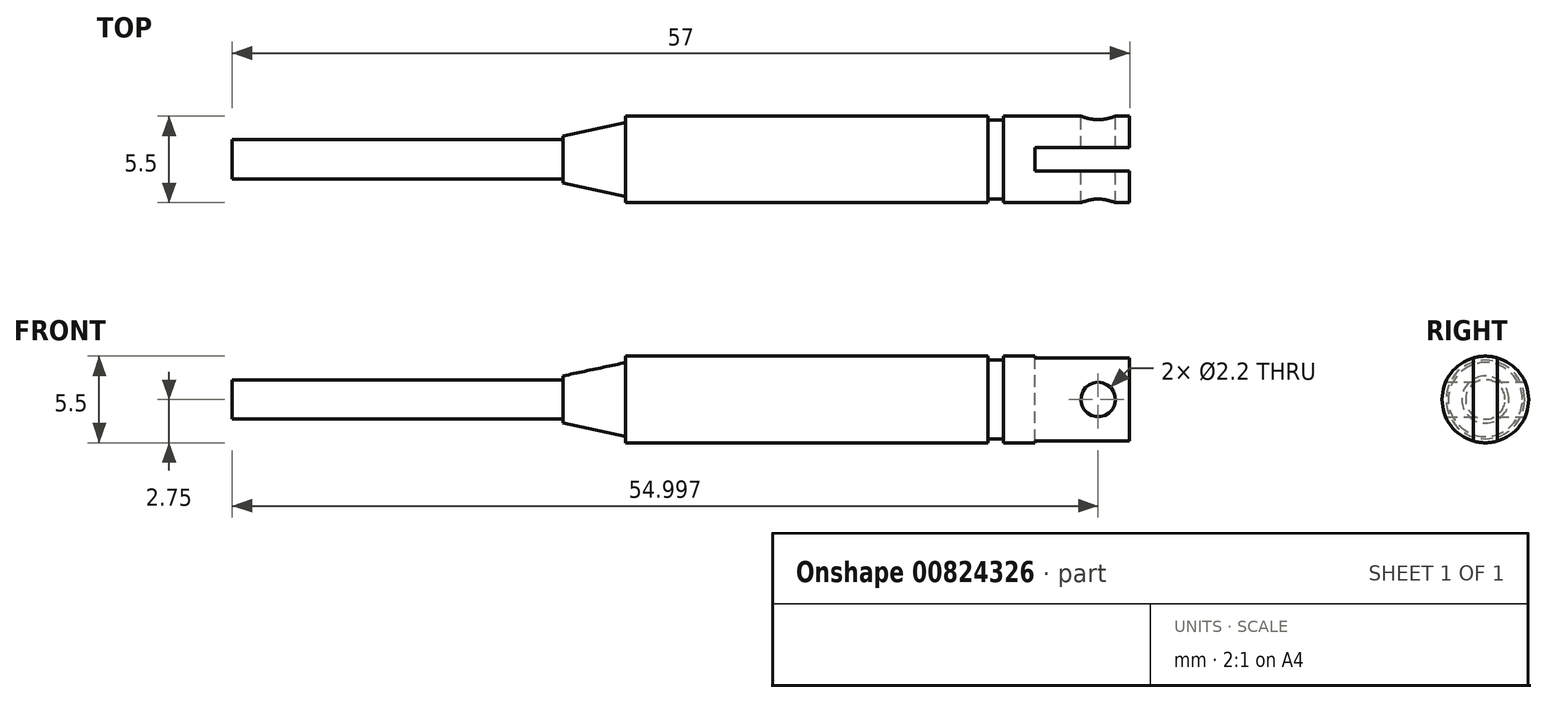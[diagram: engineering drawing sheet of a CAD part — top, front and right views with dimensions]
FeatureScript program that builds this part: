
annotation { "Feature Type Name" : "Feature", "Feature Type Description" : "" }
export const myFeature = defineFeature(function(context is Context, id is Id, definition is map)
    precondition{}
    {
        {
            var Q0;
            Q0=qCreatedBy(makeId("Front.planeOp"),FACE);
            var sketch = newSketch(context, id + "F0", { "sketchPlane" : qUnion([Q0])});
            skLineSegment(sketch, "E0.bottom", {"start": v(-27.2, 2.75) * mm, "end": v(-2.2, 2.75) * mm, "construction": true});
            skLineSegment(sketch, "E0.top", {"start": v(-27.2, 0) * mm, "end": v(29.8, 0) * mm});
            skLineSegment(sketch, "E0.left", {"start": v(-27.2, 2.75) * mm, "end": v(-27.2, 1.25) * mm, "construction": true});
            skLineSegment(sketch, "E0.right", {"start": v(29.8, 2.75) * mm, "end": v(29.8, 0) * mm});
            skLineSegment(sketch, "E1", {"start": v(-2.2, 2.75) * mm, "end": v(-2.2, 2.35) * mm});
            skLineSegment(sketch, "E2.bottom", {"start": v(-27.2, 1.25) * mm, "end": v(-27.2, 1.25) * mm});
            skLineSegment(sketch, "E2.top", {"start": v(-27.2, 0) * mm, "end": v(-2.2, 0) * mm});
            skLineSegment(sketch, "E2.left", {"start": v(-27.2, 1.25) * mm, "end": v(-27.2, 0) * mm});
            skLineSegment(sketch, "E2.right", {"start": v(-2.2, 1.25) * mm, "end": v(-2.2, 0) * mm});
            skLineSegment(sketch, "E3", {"start": v(-6.2, 1.25) * mm, "end": v(-6.2, 1.5) * mm});
            skLineSegment(sketch, "E4", {"start": v(-6.2, 1.5) * mm, "end": v(-2.2, 2.35) * mm});
            skLineSegment(sketch, "E5", {"start": v(-6.2, 1.25) * mm, "end": v(-2.2, 1.25) * mm, "construction": true});
            skLineSegment(sketch, "E6", {"start": v(-2.2, 2.35) * mm, "end": v(-2.2, 0) * mm, "construction": true});
            skLineSegment(sketch, "E7", {"start": v(-27.2, 1.25) * mm, "end": v(-6.2, 1.25) * mm});
            skLineSegment(sketch, "E8", {"start": v(29.8, 2.75) * mm, "end": v(21.8, 2.75) * mm});
            skLineSegment(sketch, "E9", {"start": v(20.8, 2.75) * mm, "end": v(-2.2, 2.75) * mm});
            skLineSegment(sketch, "E10", {"start": v(21.8, 2.75) * mm, "end": v(21.8, 2.5) * mm});
            skLineSegment(sketch, "E11", {"start": v(21.8, 2.5) * mm, "end": v(20.8, 2.5) * mm});
            skLineSegment(sketch, "E12", {"start": v(20.8, 2.5) * mm, "end": v(20.8, 2.75) * mm});
            skSolve(sketch);
        }
        {
            var Q0;
            Q0 = qSketchRegion(id + "F0", true);
            var Q1;
            Q1=sQuery(id+"F0.wireOp",EDGE,"E0.top");
            revolve(context, id + "F1", {"surfaceOperationType" : NewSurfaceOperationType.NEW, "entities" : qUnion([Q0]), "axis" : qUnion([Q1]), "revolveType" : RevolveType.FULL});
        }
        {
            var Q0;
            Q0=makeQuery(id+"F1.opRevolve","SWEPT_FACE",FACE,{"disambiguationData":[OSD([sQuery(id+"F0.wireOp",EDGE,"E0.right")])]});
            var sketch = newSketch(context, id + "F2", { "sketchPlane" : qUnion([Q0])});
            skCircle(sketch, "E13", {"center": v(0, 0) * mm, "radius": 0.75 * mm, "construction": true});
            skLineSegment(sketch, "E14", {"start": v(-0.75, 0) * mm, "end": v(-0.75, 2.65) * mm});
            skLineSegment(sketch, "E15", {"start": v(0.75, 0) * mm, "end": v(0.75, 2.65) * mm});
            skLineSegment(sketch, "E16", {"start": v(-0.75, 0) * mm, "end": v(-0.75, -2.65) * mm});
            skLineSegment(sketch, "E17", {"start": v(0.75, 0) * mm, "end": v(0.75, -2.65) * mm});
            skSolve(sketch);
        }
        {
            var Q0;
            {var subQ3=sQuery(id+"F2.wireOp",EDGE,"E14");Q0=makeQuery(id+"F2.imprint","IMPRINT",FACE,{"disambiguationData":[TD([[makeQuery(id+"F2.imprint","IMPRINT",EDGE,{"derivedFrom":subQ3}),-1.0]])]});}
            extrude(context, id + "F3", {"entities" : qUnion([Q0]), "operationType" : NewBodyOperationType.REMOVE, "oppositeDirection" : true, "depth" : 6 * mm, "offsetDistance" : 25 * mm});
        }
        {
            var Q0;
            Q0=qCreatedBy(makeId("Front.planeOp"),FACE);
            var sketch = newSketch(context, id + "F4", { "sketchPlane" : qUnion([Q0])});
            skCircle(sketch, "E18", {"center": v(27.8, 0) * mm, "radius": 1.1 * mm});
            skSolve(sketch);
        }
        {
            var Q0;
            Q0=makeQuery(id+"F4.imprint","IMPRINT",FACE,{"disambiguationData":[TD([[makeQuery(id+"F4.imprint","IMPRINT",EDGE,{"derivedFrom":sQuery(id+"F4.wireOp",EDGE,"E18")}),1.0]])]});
            extrude(context, id + "F5", {"entities" : qUnion([Q0]), "operationType" : NewBodyOperationType.REMOVE, "flatOperationType" : FlatOperationType.REMOVE, "endBound" : BoundingType.THROUGH_ALL, "depth" : 5 * mm, "offsetDistance" : 25 * mm, "hasSecondDirection" : true, "secondDirectionBound" : SecondDirectionBoundingType.THROUGH_ALL, "secondDirectionOppositeDirection" : true, "secondDirectionDepth" : 25 * mm, "domain" : OperationDomain.MODEL});
        }
    });
